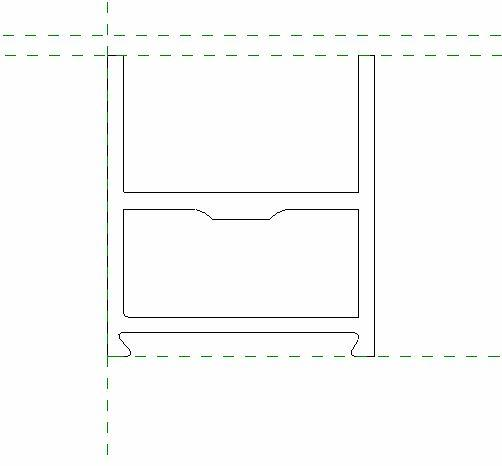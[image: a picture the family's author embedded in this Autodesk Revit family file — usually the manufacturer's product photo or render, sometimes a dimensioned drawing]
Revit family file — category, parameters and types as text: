
# Revit family: ASSA_ABLOY_VersaMax_TelescopicOHC_FBO03
name_source: partatom
category: Doors
units: mm (PartAtom-declared; Revit-internal decimal feet)

## family parameters
Always vertical = Yes
Cut with Voids When Loaded = No
Host = Wall
OmniClass Number = 23.30.10.00
OmniClass Title = Doors
Room Calculation Point = No
Shared = No

## types (3) — shared parameters
Analytic Construction = <None>
BIMobject category = Sliding Doors
Bottom Profile Height = Fix Leaf1 : 0'4''
Bottom Profile Option 01 = Fix Leaf1 : 0'4''
Bottom Profile Option 02 = Fix Leaf1 : 0'7''
Bottom Profile Option 03 = Fix Leaf1 : 0'10''
Brass Polished Finish = Brass, Polished
Brass Satin Finish = Brass, Satin
Clear Anodized = Clear Anodized
Dark Bronze Anodized = Dark Bronze Anodized
Date of publishing = 2015-02-23
Depth = 0.00
Edition number = 1
Frame Material = Clear Anodized
Function = Interior
Gap = 6.4 mm
Glass = Glass
Height = 2279.7 mm
IFC Classification = Door
Leaf Height = 2152.7 mm
Manufacturer = ASSA ABLOY Entrance Systems-North America
Manufacturer name = ASSA ABLOY Entrance Systems-North America
Material main = Aluminium
NBS Reference Code = 25-30-20-77
NBS Reference Description = Sliding Doorset Systems
Nominal height = 0.00
Nominal width = 0.00
Product SKU = VersaMax_Tele_OHC
Product data url = http://besam-na.bimobject.com
Product family = ICU
Product group = Telescopic
QR code = http://besam-na.bimobject.com
Rough Height = 2286 mm  [stored 7.5 ft]
Stainless Steel Polished Finish = Stainless Steel, Polished
Stainless Steel Satin Finish = Stainless Steel, Satin
Thickness = 152.4 mm  [stored 0.5 ft]
Top Profile Height = 101.6 mm  [stored 0.333333 ft]
UNSPSC Code = 301715
Uniclass 1.4 Code = L4133
Uniclass 1.4 Description = Sliding
Uniclass 2.0 Code = SS-25-30-20-77
Uniclass 2.0 Description = Sliding Doorset Systems
Wall Closure = By host
Weight Net (Kg) = 0

## per-type parameters (varying)
| type | Rough Width | Width |
| ICU-TE-6FBO-10 | 3060.7 mm  [stored 10.0417 ft] | 3048 mm  [stored 10 ft] |
| ICU-TE-6FBO-12 | 3670.3 mm  [stored 12.0417 ft] | 3657.6 mm  [stored 12 ft] |
| ICU-TE-6FBO-14 | 4279.9 mm | 4267.2 mm  [stored 14 ft] |

note: [stored X ft] marks values corroborated as IEEE doubles in the binary element streams (Revit-internal decimal feet)

## geometry (parser evidence)
native form markers: Sweep x40
no freeform markers — native parametric forms only
